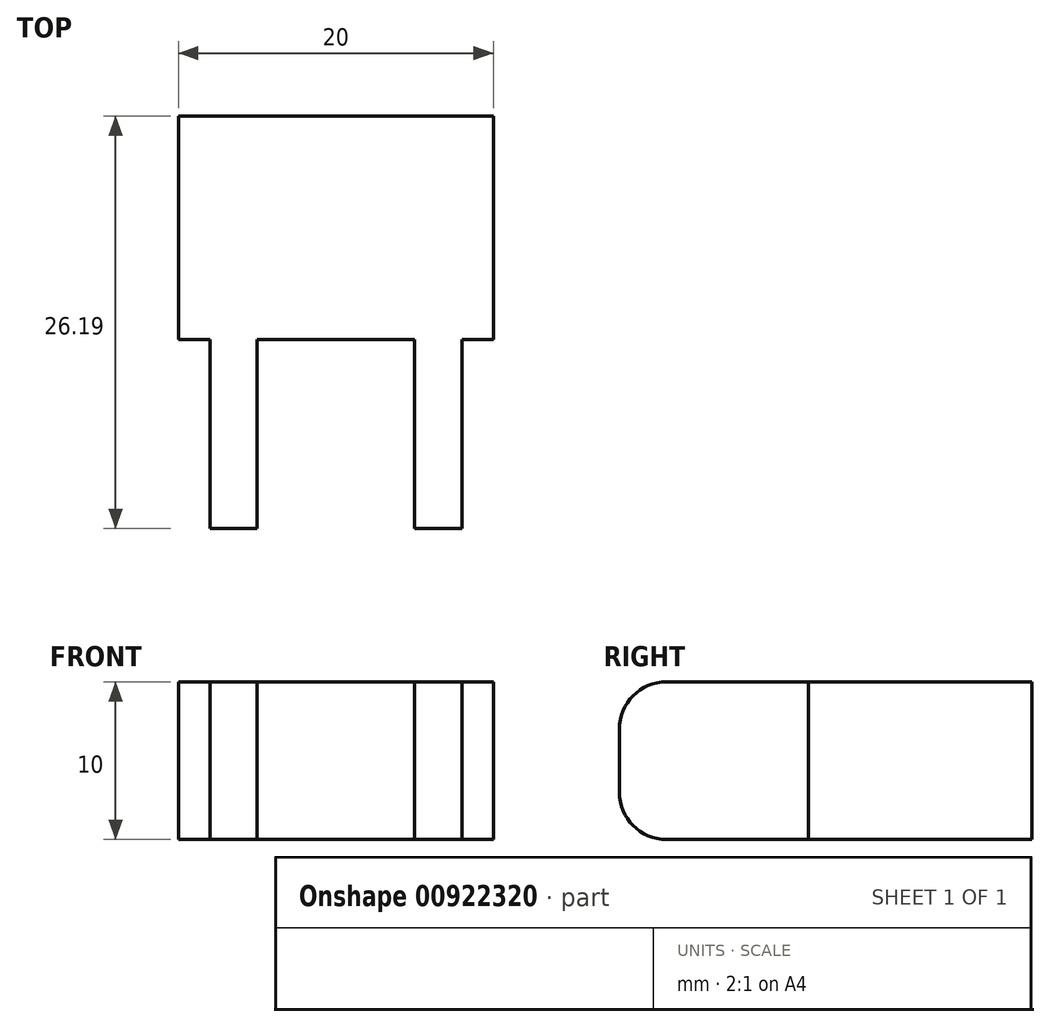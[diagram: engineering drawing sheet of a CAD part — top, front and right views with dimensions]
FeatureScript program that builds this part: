
annotation { "Feature Type Name" : "Feature", "Feature Type Description" : "" }
export const myFeature = defineFeature(function(context is Context, id is Id, definition is map)
    precondition{}
    {
        {
            var Q0;
            Q0=qCreatedBy(makeId("Top.planeOp"),FACE);
            var sketch = newSketch(context, id + "F0", { "sketchPlane" : qUnion([Q0])});
            skLineSegment(sketch, "E0", {"start": v(0, 32.76) * mm, "end": v(0, -33.66) * mm, "construction": true});
            skLineSegment(sketch, "E1", {"start": v(0, 0) * mm, "end": v(-5, 0) * mm});
            skLineSegment(sketch, "E2", {"start": v(-5, 0) * mm, "end": v(-5, -12) * mm});
            skLineSegment(sketch, "E3", {"start": v(-5, -12) * mm, "end": v(-8, -12) * mm});
            skLineSegment(sketch, "E4", {"start": v(-8, -12) * mm, "end": v(-8, 0) * mm});
            skLineSegment(sketch, "E5", {"start": v(-8, 0) * mm, "end": v(-10, 0) * mm});
            skLineSegment(sketch, "E6", {"start": v(-10, 0) * mm, "end": v(-10, 14.19) * mm});
            skLineSegment(sketch, "E7", {"start": v(-10, 14.19) * mm, "end": v(0, 14.19) * mm});
            skLineSegment(sketch, "E8.MirrorCS", {"start": v(5, -12) * mm, "end": v(8, -12) * mm});
            skLineSegment(sketch, "E9.MirrorCS", {"start": v(8, 0) * mm, "end": v(10, 0) * mm});
            skLineSegment(sketch, "E10.MirrorCS", {"start": v(10, 14.19) * mm, "end": v(0, 14.19) * mm});
            skLineSegment(sketch, "E11.MirrorCS", {"start": v(10, 0) * mm, "end": v(10, 14.19) * mm});
            skLineSegment(sketch, "E12.MirrorCS", {"start": v(8, -12) * mm, "end": v(8, 0) * mm});
            skLineSegment(sketch, "E13.MirrorCS", {"start": v(0, 0) * mm, "end": v(5, 0) * mm});
            skLineSegment(sketch, "E14.MirrorCS", {"start": v(5, 0) * mm, "end": v(5, -12) * mm});
            skSolve(sketch);
        }
        {
            var Q0;
            Q0 = qSketchRegion(id + "F0", true);
            extrude(context, id + "F1", {"entities" : qUnion([Q0]), "depth" : 10 * mm, "offsetDistance" : 25 * mm});
        }
        {
            var Q0;
            Q0=makeQuery(id+"F1.opExtrude","CAP_EDGE",EDGE,{"disambiguationData":[OSD([sQuery(id+"F0.wireOp",EDGE,"E8.MirrorCS")])],"isStart":true});
            var Q1;
            Q1=makeQuery(id+"F1.opExtrude","CAP_EDGE",EDGE,{"disambiguationData":[OSD([sQuery(id+"F0.wireOp",EDGE,"E8.MirrorCS")])],"isStart":false});
            var Q2;
            Q2=makeQuery(id+"F1.opExtrude","CAP_EDGE",EDGE,{"disambiguationData":[OSD([sQuery(id+"F0.wireOp",EDGE,"E3")])],"isStart":true});
            var Q3;
            Q3=makeQuery(id+"F1.opExtrude","CAP_EDGE",EDGE,{"disambiguationData":[OSD([sQuery(id+"F0.wireOp",EDGE,"E3")])],"isStart":false});
            fillet(context, id + "F2", {"entities" : qUnion([Q0, Q1, Q2, Q3]), "radius" : 3 * mm, "tangentPropagation" : true, "allowEdgeOverflow" : false});
        }
    });
